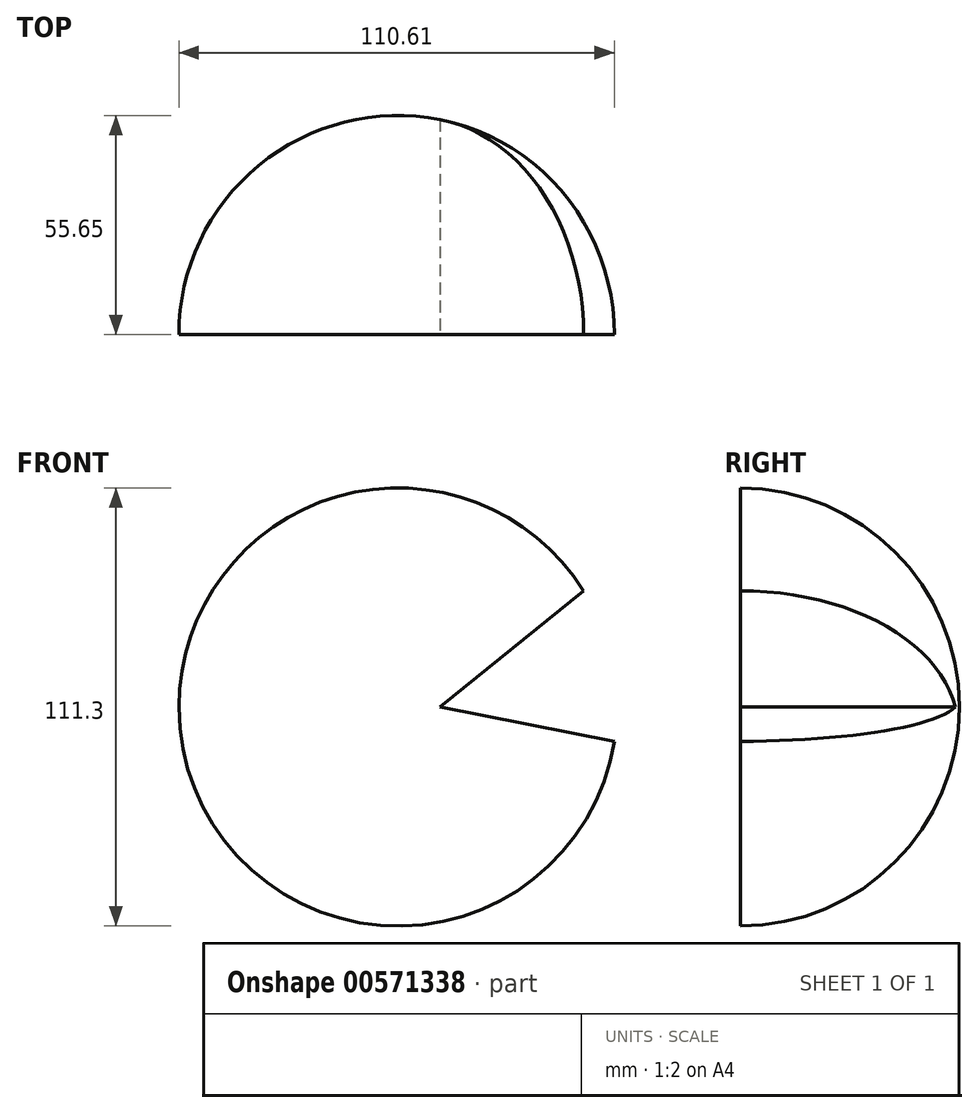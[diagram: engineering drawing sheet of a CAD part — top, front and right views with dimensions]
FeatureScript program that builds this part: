
annotation { "Feature Type Name" : "Feature", "Feature Type Description" : "" }
export const myFeature = defineFeature(function(context is Context, id is Id, definition is map)
    precondition{}
    {
        {
            var Q0;
            Q0=qCreatedBy(makeId("Front.planeOp"),FACE);
            var sketch = newSketch(context, id + "F0", { "sketchPlane" : qUnion([Q0])});
            skCircle(sketch, "E0", {"center": v(0, 0) * mm, "radius": 55.65 * mm});
            skLineSegment(sketch, "E1", {"start": v(-55.65, 0) * mm, "end": v(55.65, 0) * mm});
            skSolve(sketch);
        }
        {
            var Q0;
            {var subQ0=sQuery(id+"F0.wireOp",EDGE,"E1");Q0=makeQuery(id+"F0.imprint","IMPRINT",FACE,{"disambiguationData":[TD([[makeQuery(id+"F0.imprint","IMPRINT",EDGE,{"derivedFrom":subQ0}),-1.0]])]});}
            var Q1;
            Q1=sQuery(id+"F0.wireOp",EDGE,"E1");
            revolve(context, id + "F1", {"entities" : qUnion([Q0]), "axis" : qUnion([Q1]), "revolveType" : RevolveType.FULL});
        }
        {
            var Q0;
            Q0=qCreatedBy(makeId("Front.planeOp"),FACE);
            var sketch = newSketch(context, id + "F2", { "sketchPlane" : qUnion([Q0])});
            skPoint(sketch, "E2.start.orphan", {"position": v(0, 44.5) * mm});
            skLineSegment(sketch, "E3", {"start": v(10.72, 0) * mm, "end": v(58.58, 38.74) * mm});
            skLineSegment(sketch, "E4", {"start": v(10.72, 0) * mm, "end": v(70.82, -11.85) * mm});
            skLineSegment(sketch, "E5", {"start": v(58.58, 38.74) * mm, "end": v(70.82, -11.85) * mm});
            skSolve(sketch);
        }
        {
            var Q0;
            Q0 = qSketchRegion(id + "F2", true);
            extrude(context, id + "F3", {"entities" : qUnion([Q0]), "operationType" : NewBodyOperationType.REMOVE, "endBound" : BoundingType.THROUGH_ALL, "oppositeDirection" : true, "depth" : 25.4 * mm, "offsetDistance" : 25.4 * mm, "hasSecondDirection" : true, "secondDirectionBound" : SecondDirectionBoundingType.THROUGH_ALL, "secondDirectionOppositeDirection" : false, "secondDirectionDepth" : 25.4 * mm});
        }
        {
            var Q0;
            Q0=qCreatedBy(makeId("Top.planeOp"),FACE);
            var sketch = newSketch(context, id + "F4", { "sketchPlane" : qUnion([Q0])});
            skLineSegment(sketch, "E6", {"start": v(-63.64, 0) * mm, "end": v(71.62, 0) * mm});
            skLineSegment(sketch, "E7", {"start": v(71.62, 0) * mm, "end": v(71.62, -69.36) * mm});
            skLineSegment(sketch, "E8", {"start": v(71.62, -69.36) * mm, "end": v(-62.3, -69.36) * mm});
            skLineSegment(sketch, "E9", {"start": v(-62.3, -69.36) * mm, "end": v(-63.64, 0) * mm});
            skSolve(sketch);
        }
        {
            var Q0;
            Q0=makeQuery(id+"F4.imprint","IMPRINT",FACE,{"disambiguationData":[TD([[makeQuery(id+"F4.imprint","IMPRINT",EDGE,{"derivedFrom":sQuery(id+"F4.wireOp",EDGE,"E6")}),-1.0]])]});
            extrude(context, id + "F5", {"entities" : qUnion([Q0]), "operationType" : NewBodyOperationType.REMOVE, "endBound" : BoundingType.THROUGH_ALL, "oppositeDirection" : true, "depth" : 25.4 * mm, "offsetDistance" : 25.4 * mm, "hasSecondDirection" : true, "secondDirectionBound" : SecondDirectionBoundingType.THROUGH_ALL, "secondDirectionOppositeDirection" : false, "secondDirectionDepth" : 25.4 * mm});
        }
    });
